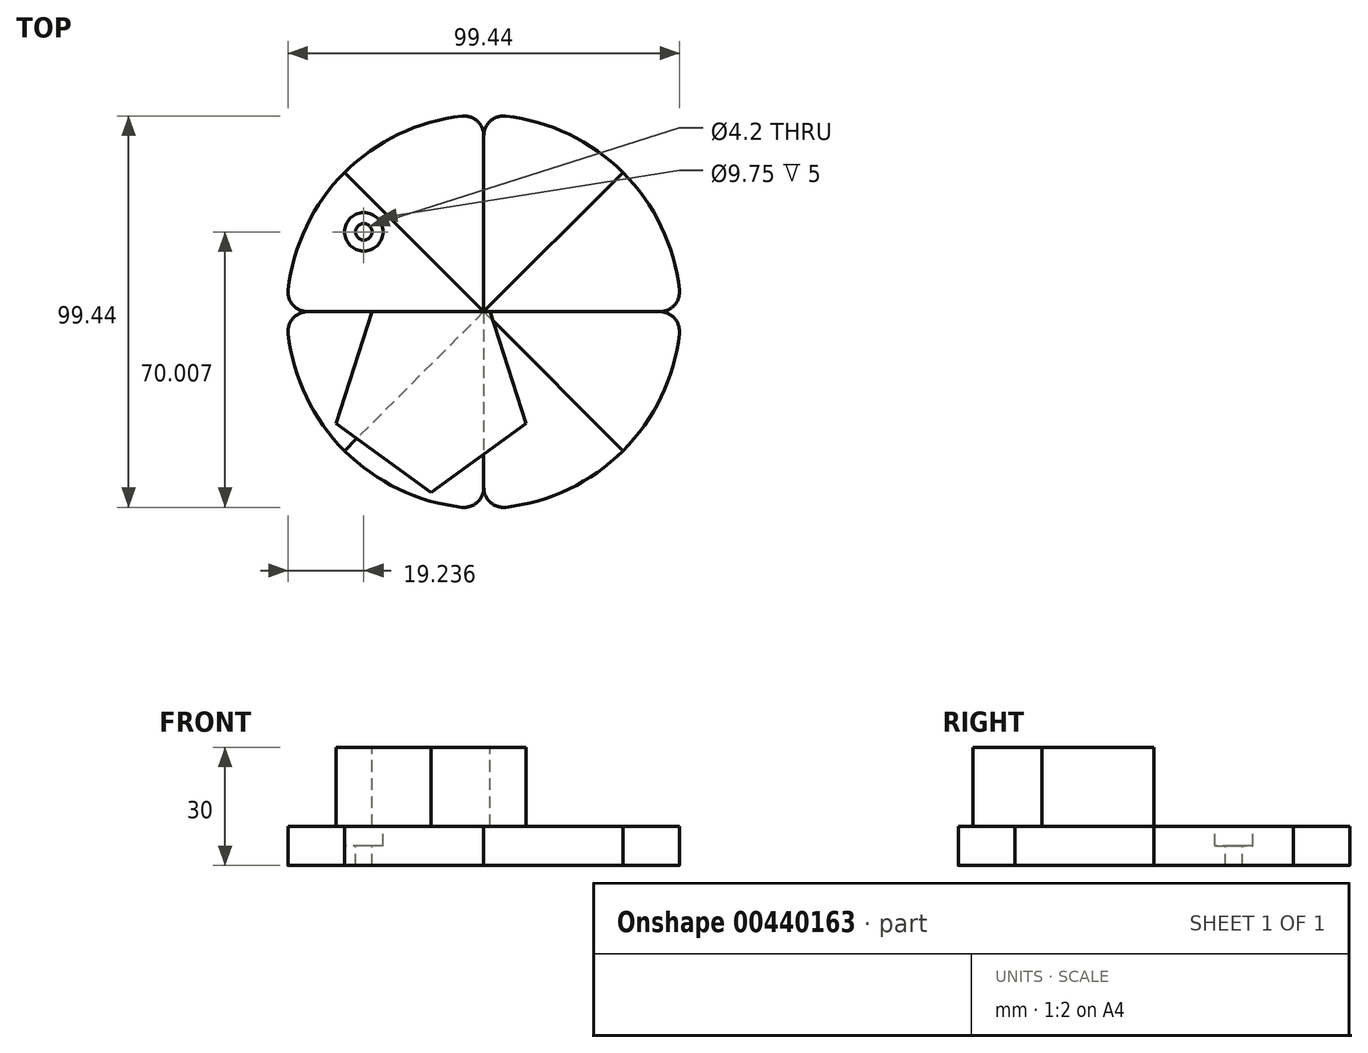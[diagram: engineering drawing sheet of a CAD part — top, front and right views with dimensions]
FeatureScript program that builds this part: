
annotation { "Feature Type Name" : "Feature", "Feature Type Description" : "" }
export const myFeature = defineFeature(function(context is Context, id is Id, definition is map)
    precondition{}
    {
        {
            var Q0;
            Q0=qCreatedBy(makeId("Top.planeOp"),FACE);
            var sketch = newSketch(context, id + "F0", { "sketchPlane" : qUnion([Q0])});
            skArc(sketch, "E0", {"start": v(35.36, 35.36) * mm, "mid": v(19.13, 46.2) * mm, "end": v(0, 50) * mm});
            skLineSegment(sketch, "E1", {"start": v(0, 0) * mm, "end": v(50, 0) * mm});
            skLineSegment(sketch, "E2.1.0", {"start": v(0, 0) * mm, "end": v(35.36, 35.36) * mm});
            skLineSegment(sketch, "E2.2.0", {"start": v(0, 0) * mm, "end": v(0, 50) * mm});
            skLineSegment(sketch, "E2.3.0", {"start": v(0, 0) * mm, "end": v(-35.36, 35.36) * mm});
            skLineSegment(sketch, "E2.4.0", {"start": v(0, 0) * mm, "end": v(-50, 0) * mm});
            skLineSegment(sketch, "E2.5.0", {"start": v(0, 0) * mm, "end": v(-35.36, -35.36) * mm});
            skLineSegment(sketch, "E2.6.0", {"start": v(0, 0) * mm, "end": v(0, -50) * mm});
            skLineSegment(sketch, "E2.7.0", {"start": v(0, 0) * mm, "end": v(35.36, -35.36) * mm});
            skArc(sketch, "E3.trimOffspring", {"start": v(-35.36, 35.36) * mm, "mid": v(-46.2, 19.13) * mm, "end": v(-50, 0) * mm});
            skArc(sketch, "E4.trimOffspring", {"start": v(-35.36, -35.36) * mm, "mid": v(-19.13, -46.2) * mm, "end": v(0, -50) * mm});
            skArc(sketch, "E5.trimOffspring", {"start": v(35.36, -35.36) * mm, "mid": v(46.2, -19.13) * mm, "end": v(50, 0) * mm});
            skSolve(sketch);
        }
        {
            var Q0;
            Q0 = qSketchRegion(id + "F0", true);
            extrude(context, id + "F1", {"entities" : qUnion([Q0]), "depth" : 10 * mm});
        }
        {
            var Q0;
            Q0=makeQuery(id+"F1.opExtrude","SWEPT_EDGE",EDGE,{"disambiguationData":[OSD([sQuery(id+"F0.wireOp",EDGE,"E1"),sQuery(id+"F0.wireOp",EDGE,"E5.trimOffspring")])]});
            var Q1;
            Q1=makeQuery(id+"F1.opExtrude","SWEPT_EDGE",EDGE,{"disambiguationData":[OSD([sQuery(id+"F0.wireOp",EDGE,"E0"),sQuery(id+"F0.wireOp",EDGE,"E2.2.0")])]});
            var Q2;
            Q2=makeQuery(id+"F1.opExtrude","SWEPT_EDGE",EDGE,{"disambiguationData":[OSD([sQuery(id+"F0.wireOp",EDGE,"E2.4.0"),sQuery(id+"F0.wireOp",EDGE,"E3.trimOffspring")])]});
            var Q3;
            Q3=makeQuery(id+"F1.opExtrude","SWEPT_EDGE",EDGE,{"disambiguationData":[OSD([sQuery(id+"F0.wireOp",EDGE,"E2.6.0"),sQuery(id+"F0.wireOp",EDGE,"E4.trimOffspring")])]});
            fillet(context, id + "F2", {"entities" : qUnion([Q0, Q1, Q2, Q3]), "radius" : 5 * mm, "tangentPropagation" : true, "allowEdgeOverflow" : false});
        }
        {
            var Q0;
            Q0=makeQuery(id+"F1.opExtrude","CAP_FACE",FACE,{"disambiguationData":[OSD([sQuery(id+"F0.wireOp",EDGE,"E2.3.0"),sQuery(id+"F0.wireOp",EDGE,"E2.4.0"),sQuery(id+"F0.wireOp",EDGE,"E3.trimOffspring")])],"isStart":false});
            var sketch = newSketch(context, id + "F3", { "sketchPlane" : qUnion([Q0])});
            skPoint(sketch, "E6", {"position": v(-30.48, 20.29) * mm});
            skSolve(sketch);
        }
        {
            var Q0;
            Q0=sQuery(id+"F3.wireOp",VERTEX,"E6");
            var Q1;
            Q1=makeQuery(id+"F1.opExtrude","SWEPT_BODY",BODY,{"disambiguationData":[OSD([sQuery(id+"F0.wireOp",EDGE,"E2.3.0"),sQuery(id+"F0.wireOp",EDGE,"E2.4.0"),sQuery(id+"F0.wireOp",EDGE,"E3.trimOffspring")])]});
            hole(context, id + "F4", {"style" : HoleStyle.C_BORE, "endStyle" : HoleEndStyle.THROUGH, "standardTappedOrClearance" : lookupTablePath({ "standard" : "ISO", "engagement" : "75%", "pitch" : "0.8 mm", "size" : "M5", "type" : "Tapped" }), "standardBlindInLast" : lookupTablePath({ "standard" : "ISO", "engagement" : "75%", "pitch" : "0.8 mm", "size" : "M5", "type" : "Tapped" }), "holeDiameter" : 4.2 * mm, "cBoreDiameter" : 9.75 * mm, "cBoreDepth" : 5 * mm, "showTappedDepth" : true, "isTappedThrough" : true, "tappedDepth" : 12 * mm, "tapClearance" : 3, "locations" : qUnion([Q0]), "scope" : qUnion([Q1]), "majorDiameter" : 5 * mm});
        }
        {
            var Q0;
            Q0=makeQuery(id+"F1.opExtrude","SWEPT_BODY",BODY,{"disambiguationData":[OSD([sQuery(id+"F0.wireOp",EDGE,"E0"),sQuery(id+"F0.wireOp",EDGE,"E2.1.0"),sQuery(id+"F0.wireOp",EDGE,"E2.2.0")])]});
            var Q1;
            Q1=makeQuery(id+"F1.opExtrude","SWEPT_FACE",FACE,{"disambiguationData":[OSD([sQuery(id+"F0.wireOp",EDGE,"E2.2.0")])]});
            mirror(context, id + "F5", {"entities" : qUnion([Q0]), "mirrorPlane" : qUnion([Q1])});
        }
        {
            var Q0;
            Q0=makeQuery(id+"F5.opPattern","COPY",BODY,{"derivedFrom":makeQuery(id+"F1.opExtrude","SWEPT_BODY",BODY,{"disambiguationData":[OSD([sQuery(id+"F0.wireOp",EDGE,"E0"),sQuery(id+"F0.wireOp",EDGE,"E2.1.0"),sQuery(id+"F0.wireOp",EDGE,"E2.2.0")])]}),"instanceName":"1"});
            var Q1;
            Q1=makeQuery(id+"F1.opExtrude","SWEPT_EDGE",EDGE,{"disambiguationData":[OSD([sQuery(id+"F0.wireOp",EDGE,"E1"),sQuery(id+"F0.wireOp",EDGE,"E2.1.0"),sQuery(id+"F0.wireOp",EDGE,"E2.2.0"),sQuery(id+"F0.wireOp",EDGE,"E2.3.0"),sQuery(id+"F0.wireOp",EDGE,"E2.4.0"),sQuery(id+"F0.wireOp",EDGE,"E2.5.0"),sQuery(id+"F0.wireOp",EDGE,"E2.6.0"),sQuery(id+"F0.wireOp",EDGE,"E2.7.0")]),OD(2.0)]});
            circularPattern(context, id + "F6", {"entities" : qUnion([Q0]), "axis" : qUnion([Q1]), "angle" : 360 * degree, "instanceCount" : 4, "equalSpace" : true});
        }
        {
            var Q0;
            Q0=makeQuery(id+"F1.opExtrude","CAP_FACE",FACE,{"disambiguationData":[OSD([sQuery(id+"F0.wireOp",EDGE,"E2.5.0"),sQuery(id+"F0.wireOp",EDGE,"E2.6.0"),sQuery(id+"F0.wireOp",EDGE,"E4.trimOffspring")])],"isStart":false});
            cPlane(context, id + "F7", {"entities" : qUnion([Q0]), "cplaneType" : CPlaneType.OFFSET, "offset" : 20 * mm, "width" : 150 * mm, "height" : 150 * mm});
        }
        {
            var Q0;
            Q0=qCreatedBy(id+"F7.planeOp",FACE);
            var sketch = newSketch(context, id + "F8", { "sketchPlane" : qUnion([Q0])});
            skCircle(sketch, "E7.cCircle", {"center": v(-13.38, -20.56) * mm, "radius": 20.56 * mm, "construction": true});
            skLineSegment(sketch, "E7.0", {"start": v(-28.32, 0) * mm, "end": v(1.56, 0) * mm});
            skLineSegment(sketch, "E7.1", {"start": v(1.56, 0) * mm, "end": v(10.8, -28.42) * mm});
            skLineSegment(sketch, "E7.2", {"start": v(10.8, -28.42) * mm, "end": v(-13.38, -45.98) * mm});
            skLineSegment(sketch, "E7.3", {"start": v(-13.38, -45.98) * mm, "end": v(-37.55, -28.42) * mm});
            skLineSegment(sketch, "E7.4", {"start": v(-37.55, -28.42) * mm, "end": v(-28.32, 0) * mm});
            skPoint(sketch, "E7.0.midPoint", {"position": v(-13.38, 0) * mm});
            skSolve(sketch);
        }
        {
            var Q0;
            Q0 = qSketchRegion(id + "F8", true);
            var Q1;
            Q1=makeQuery(id+"F6.opPattern","COPY",FACE,{"derivedFrom":makeQuery(id+"F5.opPattern","COPY",FACE,{"derivedFrom":makeQuery(id+"F1.opExtrude","CAP_FACE",FACE,{"disambiguationData":[OSD([sQuery(id+"F0.wireOp",EDGE,"E0"),sQuery(id+"F0.wireOp",EDGE,"E2.1.0"),sQuery(id+"F0.wireOp",EDGE,"E2.2.0")])],"isStart":false}),"instanceName":"1"}),"instanceName":"2"});
            extrude(context, id + "F9", {"entities" : qUnion([Q0]), "endBound" : BoundingType.UP_TO_SURFACE, "oppositeDirection" : true, "endBoundEntityFace" : qUnion([Q1]), "depth" : 47.2 * mm});
        }
    });
